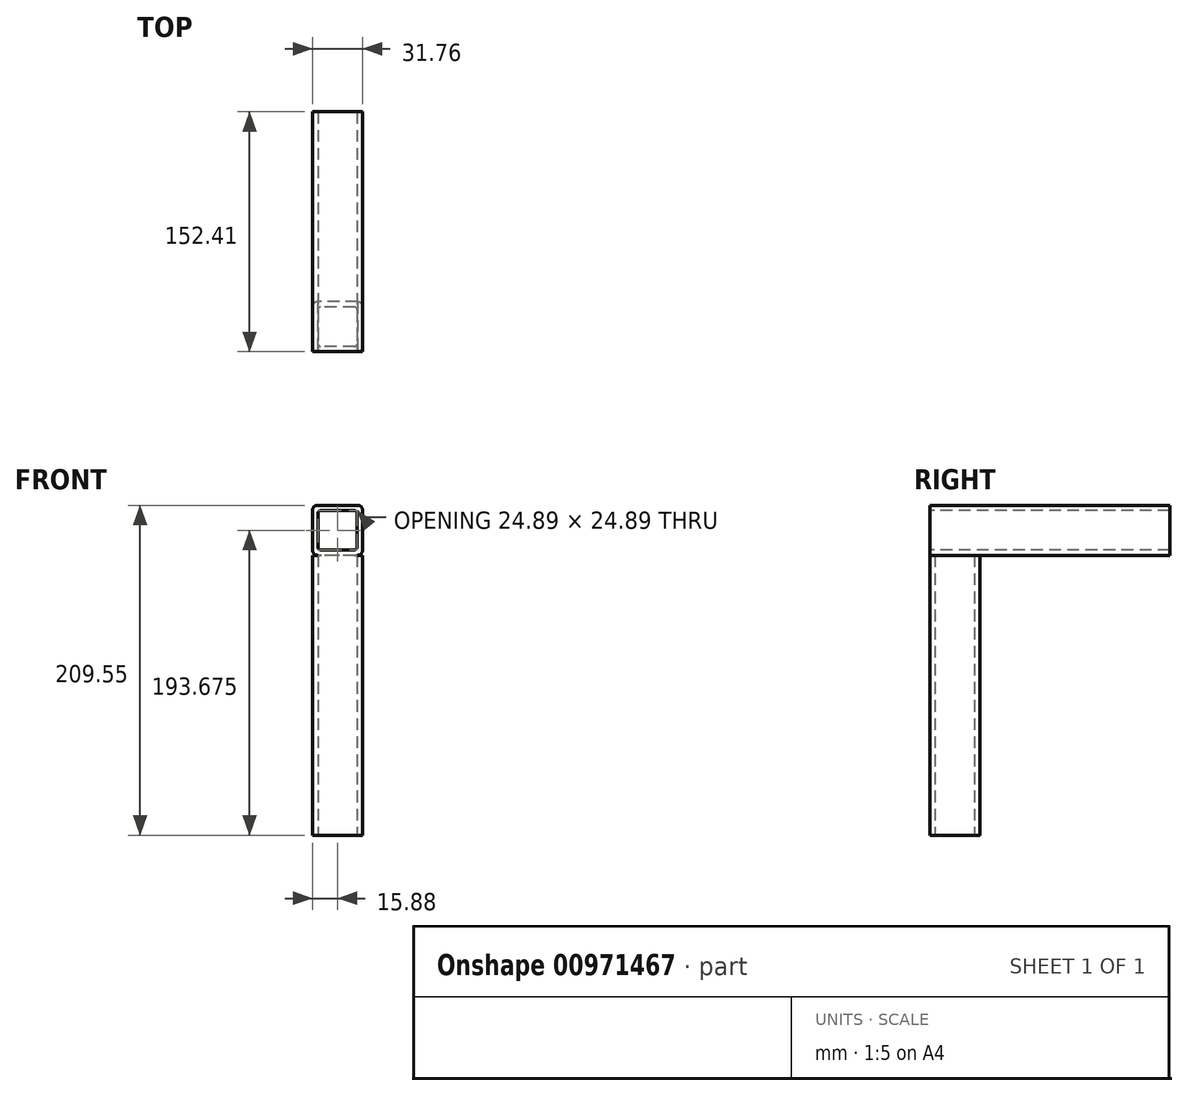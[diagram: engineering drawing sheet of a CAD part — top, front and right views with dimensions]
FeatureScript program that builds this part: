
annotation { "Feature Type Name" : "Feature", "Feature Type Description" : "" }
export const myFeature = defineFeature(function(context is Context, id is Id, definition is map)
    precondition{}
    {
        {
            var Q0;
            Q0=qCreatedBy(makeId("Top.planeOp"),FACE);
            var sketch = newSketch(context, id + "F0", { "sketchPlane" : qUnion([Q0])});
            skLineSegment(sketch, "E0.bottom", {"start": v(12.7, 15.88) * mm, "end": v(-12.7, 15.88) * mm});
            skLineSegment(sketch, "E0.top", {"start": v(12.7, -15.88) * mm, "end": v(-12.7, -15.88) * mm});
            skLineSegment(sketch, "E0.left", {"start": v(15.87, 12.7) * mm, "end": v(15.88, -12.7) * mm});
            skLineSegment(sketch, "E0.right", {"start": v(-15.88, 12.7) * mm, "end": v(-15.87, -12.7) * mm});
            skPoint(sketch, "E0.middle", {"position": v(0, 0) * mm});
            skPoint(sketch, "E1.visualSharp", {"position": v(-15.88, 15.88) * mm});
            skArc(sketch, "E1.filletArc", {"start": v(-12.7, 15.88) * mm, "mid": v(-14.95, 14.95) * mm, "end": v(-15.88, 12.7) * mm});
            skPoint(sketch, "E2.visualSharp", {"position": v(15.87, 15.88) * mm});
            skArc(sketch, "E2.filletArc", {"start": v(15.87, 12.7) * mm, "mid": v(14.95, 14.95) * mm, "end": v(12.7, 15.88) * mm});
            skPoint(sketch, "E3.visualSharp", {"position": v(15.88, -15.88) * mm});
            skArc(sketch, "E3.filletArc", {"start": v(12.7, -15.88) * mm, "mid": v(14.95, -14.95) * mm, "end": v(15.88, -12.7) * mm});
            skPoint(sketch, "E4.visualSharp", {"position": v(-15.87, -15.88) * mm});
            skArc(sketch, "E4.filletArc", {"start": v(-15.87, -12.7) * mm, "mid": v(-14.95, -14.95) * mm, "end": v(-12.7, -15.88) * mm});
            skLineSegment(sketch, "E5.1", {"start": v(12.45, 10.86) * mm, "end": v(12.45, -10.86) * mm});
            skLineSegment(sketch, "E5.2", {"start": v(10.86, 12.45) * mm, "end": v(-10.86, 12.45) * mm});
            skLineSegment(sketch, "E5.5", {"start": v(-12.45, 10.86) * mm, "end": v(-12.45, -10.86) * mm});
            skLineSegment(sketch, "E5.7", {"start": v(10.86, -12.45) * mm, "end": v(-10.86, -12.45) * mm});
            skArc(sketch, "E6.filletArc", {"start": v(-12.45, -10.86) * mm, "mid": v(-11.98, -11.98) * mm, "end": v(-10.86, -12.45) * mm});
            skArc(sketch, "E7.filletArc", {"start": v(10.86, -12.45) * mm, "mid": v(11.98, -11.98) * mm, "end": v(12.45, -10.86) * mm});
            skArc(sketch, "E8.filletArc", {"start": v(12.45, 10.86) * mm, "mid": v(11.98, 11.98) * mm, "end": v(10.86, 12.45) * mm});
            skArc(sketch, "E9.filletArc", {"start": v(-10.86, 12.45) * mm, "mid": v(-11.98, 11.98) * mm, "end": v(-12.45, 10.86) * mm});
            skSolve(sketch);
        }
        {
            var Q0;
            Q0 = qSketchRegion(id + "F0", true);
            extrude(context, id + "F1", {"entities" : qUnion([Q0]), "depth" : 76.2 * mm, "offsetDistance" : 25.4 * mm, "hasSecondDirection" : true, "secondDirectionOppositeDirection" : true, "secondDirectionDepth" : 101.6 * mm});
        }
        {
            var Q0;
            Q0=makeQuery(id+"F1.opExtrude","SWEPT_FACE",FACE,{"disambiguationData":[OSD([sQuery(id+"F0.wireOp",EDGE,"E0.top")])]});
            var sketch = newSketch(context, id + "F2", { "sketchPlane" : qUnion([Q0])});
            skLineSegment(sketch, "E10.0", {"start": v(12.7, 76.2) * mm, "end": v(-12.7, 76.2) * mm});
            skLineSegment(sketch, "E11", {"start": v(15.88, 79.38) * mm, "end": v(15.88, 104.78) * mm});
            skLineSegment(sketch, "E12", {"start": v(12.7, 107.95) * mm, "end": v(-12.7, 107.95) * mm});
            skLineSegment(sketch, "E13", {"start": v(-15.88, 104.78) * mm, "end": v(-15.88, 79.38) * mm});
            skPoint(sketch, "E14.visualSharp", {"position": v(15.88, 76.2) * mm});
            skArc(sketch, "E14.filletArc", {"start": v(12.7, 76.2) * mm, "mid": v(14.95, 77.13) * mm, "end": v(15.87, 79.38) * mm});
            skPoint(sketch, "E15.visualSharp", {"position": v(-15.88, 76.2) * mm});
            skArc(sketch, "E15.filletArc", {"start": v(-15.87, 79.38) * mm, "mid": v(-14.95, 77.13) * mm, "end": v(-12.7, 76.2) * mm});
            skPoint(sketch, "E16.visualSharp", {"position": v(-15.88, 107.95) * mm});
            skArc(sketch, "E16.filletArc", {"start": v(-12.7, 107.95) * mm, "mid": v(-14.95, 107.02) * mm, "end": v(-15.88, 104.78) * mm});
            skPoint(sketch, "E17.visualSharp", {"position": v(15.88, 107.95) * mm});
            skArc(sketch, "E17.filletArc", {"start": v(15.87, 104.78) * mm, "mid": v(14.95, 107.02) * mm, "end": v(12.7, 107.95) * mm});
            skLineSegment(sketch, "E18.0", {"start": v(-12.45, 102.93) * mm, "end": v(-12.45, 81.22) * mm});
            skLineSegment(sketch, "E19.0", {"start": v(10.86, 104.52) * mm, "end": v(-10.86, 104.52) * mm});
            skLineSegment(sketch, "E20.0", {"start": v(12.45, 81.22) * mm, "end": v(12.45, 102.93) * mm});
            skLineSegment(sketch, "E21.0", {"start": v(10.86, 79.63) * mm, "end": v(-10.86, 79.63) * mm});
            skArc(sketch, "E22.filletArc", {"start": v(12.45, 102.93) * mm, "mid": v(11.98, 104.06) * mm, "end": v(10.86, 104.52) * mm});
            skArc(sketch, "E23.filletArc", {"start": v(10.86, 79.63) * mm, "mid": v(11.98, 80.1) * mm, "end": v(12.45, 81.22) * mm});
            skArc(sketch, "E24.filletArc", {"start": v(-12.45, 81.22) * mm, "mid": v(-11.98, 80.1) * mm, "end": v(-10.86, 79.63) * mm});
            skArc(sketch, "E25.filletArc", {"start": v(-10.86, 104.52) * mm, "mid": v(-11.98, 104.06) * mm, "end": v(-12.45, 102.93) * mm});
            skSolve(sketch);
        }
        {
            var Q0;
            Q0 = qSketchRegion(id + "F2", true);
            extrude(context, id + "F3", {"entities" : qUnion([Q0]), "operationType" : NewBodyOperationType.ADD, "oppositeDirection" : true, "depth" : 152.4 * mm, "offsetDistance" : 25.4 * mm});
        }
    });
